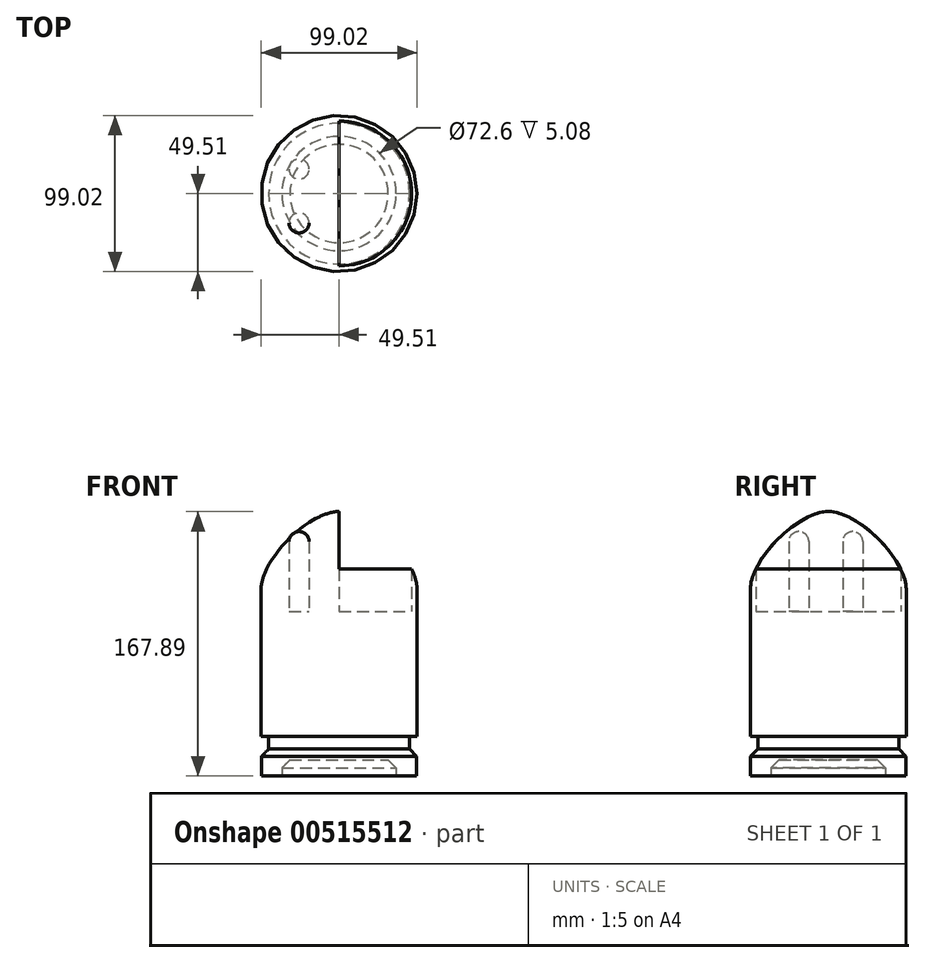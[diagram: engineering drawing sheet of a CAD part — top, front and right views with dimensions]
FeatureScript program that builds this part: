
annotation { "Feature Type Name" : "Feature", "Feature Type Description" : "" }
export const myFeature = defineFeature(function(context is Context, id is Id, definition is map)
    precondition{}
    {
        {
            var Q0;
            Q0=qCreatedBy(makeId("Top.planeOp"),FACE);
            var sketch = newSketch(context, id + "F0", { "sketchPlane" : qUnion([Q0])});
            skCircle(sketch, "E0", {"center": v(0, 0) * mm, "radius": 49.51 * mm});
            skSolve(sketch);
        }
        {
            var Q0;
            Q0=makeQuery(id+"F0.imprint","IMPRINT",FACE,{"disambiguationData":[TD([[makeQuery(id+"F0.imprint","IMPRINT",EDGE,{"derivedFrom":sQuery(id+"F0.wireOp",EDGE,"E0")}),1.0]])]});
            extrude(context, id + "F1", {"entities" : qUnion([Q0]), "endBound" : BoundingType.SYMMETRIC, "depth" : 127 * mm, "offsetDistance" : 25.4 * mm});
        }
        {
            var Q0;
            Q0=makeQuery(id+"F1.opExtrude","CAP_EDGE",EDGE,{"disambiguationData":[OSD([sQuery(id+"F0.wireOp",EDGE,"E0")])],"isStart":false});
            fillet(context, id + "F2", {"entities" : qUnion([Q0]), "radius" : 49.28 * mm, "tangentPropagation" : true, "rho" : .29, "crossSection" : FilletCrossSection.CONIC, "allowEdgeOverflow" : false});
        }
        {
            var Q0;
            Q0=makeQuery(id+"F1.opExtrude","CAP_FACE",FACE,{"disambiguationData":[OSD([sQuery(id+"F0.wireOp",EDGE,"E0")])],"isStart":true});
            extrude(context, id + "F3", {"entities" : qUnion([Q0]), "operationType" : NewBodyOperationType.ADD, "depth" : 15.75 * mm, "offsetDistance" : 25.4 * mm});
        }
        {
            var Q0;
            Q0=makeQuery(id+"F3.opExtrude","CAP_FACE",FACE,{"disambiguationData":[OSD([sQuery(id+"F0.wireOp",EDGE,"E0")])],"isStart":false});
            var sketch = newSketch(context, id + "F4", { "sketchPlane" : qUnion([Q0])});
            skCircle(sketch, "E1", {"center": v(0, 0) * mm, "radius": 44.75 * mm});
            skSolve(sketch);
        }
        {
            var Q0;
            Q0=makeQuery(id+"F4.imprint","IMPRINT",FACE,{"disambiguationData":[TD([[makeQuery(id+"F4.imprint","IMPRINT",EDGE,{"derivedFrom":sQuery(id+"F4.wireOp",EDGE,"E1")}),1.0]])]});
            extrude(context, id + "F5", {"entities" : qUnion([Q0]), "operationType" : NewBodyOperationType.ADD, "depth" : 7.62 * mm, "offsetDistance" : 25.4 * mm});
        }
        {
            var Q0;
            Q0=makeQuery(id+"F5.opExtrude","CAP_FACE",FACE,{"disambiguationData":[OSD([sQuery(id+"F4.wireOp",EDGE,"E1")])],"isStart":false});
            var sketch = newSketch(context, id + "F6", { "sketchPlane" : qUnion([Q0])});
            skCircle(sketch, "E2", {"center": v(0, 0) * mm, "radius": 49.32 * mm});
            skSolve(sketch);
        }
        {
            var Q0;
            Q0=makeQuery(id+"F6.imprint","IMPRINT",FACE,{"disambiguationData":[TD([[makeQuery(id+"F6.imprint","IMPRINT",EDGE,{"derivedFrom":makeQuery(id+"F5.opExtrude","CAP_EDGE",EDGE,{"disambiguationData":[OSD([sQuery(id+"F4.wireOp",EDGE,"E1")])],"isStart":false})}),1.0]])]});
            var Q1;
            Q1=makeQuery(id+"F6.imprint","IMPRINT",FACE,{"disambiguationData":[TD([[makeQuery(id+"F6.imprint","IMPRINT",EDGE,{"derivedFrom":sQuery(id+"F6.wireOp",EDGE,"E2")}),1.0]])]});
            extrude(context, id + "F7", {"entities" : qUnion([Q0, Q1]), "operationType" : NewBodyOperationType.ADD, "depth" : 17.53 * mm, "offsetDistance" : 25.4 * mm});
        }
        {
            var Q0;
            Q0=makeQuery(id+"F7.opExtrude","CAP_EDGE",EDGE,{"disambiguationData":[OSD([sQuery(id+"F6.wireOp",EDGE,"E2")])],"isStart":true});
            chamfer(context, id + "F8", {"entities" : qUnion([Q0]), "width" : 5.08 * mm, "tangentPropagation" : true});
        }
        {
            var Q0;
            Q0=makeQuery(id+"F7.opExtrude","CAP_FACE",FACE,{"disambiguationData":[OSD([sQuery(id+"F6.wireOp",EDGE,"E2")])],"isStart":false});
            var sketch = newSketch(context, id + "F9", { "sketchPlane" : qUnion([Q0])});
            skCircle(sketch, "E3", {"center": v(0, 0) * mm, "radius": 36.3 * mm});
            skSolve(sketch);
        }
        {
            var Q0;
            Q0=makeQuery(id+"F9.imprint","IMPRINT",FACE,{"disambiguationData":[TD([[makeQuery(id+"F9.imprint","IMPRINT",EDGE,{"derivedFrom":sQuery(id+"F9.wireOp",EDGE,"E3")}),1.0]])]});
            extrude(context, id + "F10", {"entities" : qUnion([Q0]), "operationType" : NewBodyOperationType.REMOVE, "oppositeDirection" : true, "depth" : 10.16 * mm, "offsetDistance" : 25.4 * mm});
        }
        {
            var Q0;
            Q0=makeQuery(id+"F10.boolean.opBoolean","COPY",EDGE,{"derivedFrom":makeQuery(id+"F10.opExtrude","CAP_EDGE",EDGE,{"disambiguationData":[OSD([sQuery(id+"F9.wireOp",EDGE,"E3")])],"isStart":false})});
            var Q1;
            Q1=makeQuery(id+"F10.boolean.opBoolean","COPY",EDGE,{"derivedFrom":makeQuery(id+"F10.opExtrude","CAP_EDGE",EDGE,{"disambiguationData":[OSD([sQuery(id+"F9.wireOp",EDGE,"E3")])],"isStart":true})});
            chamfer(context, id + "F11", {"entities" : qUnion([Q0, Q1]), "width" : 5.08 * mm, "tangentPropagation" : true});
        }
        {
            var Q0;
            Q0=qCreatedBy(makeId("Top.planeOp"),FACE);
            var sketch = newSketch(context, id + "F12", { "sketchPlane" : qUnion([Q0])});
            skLineSegment(sketch, "E4", {"start": v(0, -45.98) * mm, "end": v(0, 45.98) * mm});
            skArc(sketch, "E5", {"start": v(0, -45.98) * mm, "mid": v(45.98, 0) * mm, "end": v(0, 45.98) * mm});
            skSolve(sketch);
        }
        {
            var Q0;
            Q0 = qSketchRegion(id + "F12", true);
            extrude(context, id + "F13", {"entities" : qUnion([Q0]), "operationType" : NewBodyOperationType.REMOVE, "endBound" : BoundingType.THROUGH_ALL, "depth" : 25.4 * mm, "offsetDistance" : 25.4 * mm});
        }
        {
            var Q0;
            Q0=makeQuery(id+"F13.boolean.opBoolean","COPY",FACE,{"derivedFrom":makeQuery(id+"F13.opExtrude","CAP_FACE",FACE,{"disambiguationData":[OSD([sQuery(id+"F12.wireOp",EDGE,"E4"),sQuery(id+"F12.wireOp",EDGE,"E5")])],"isStart":true})});
            var sketch = newSketch(context, id + "F14", { "sketchPlane" : qUnion([Q0])});
            skCircle(sketch, "E6", {"center": v(-25.4, -18.7) * mm, "radius": 6.35 * mm});
            skCircle(sketch, "E7", {"center": v(-25.4, 15.53) * mm, "radius": 6.35 * mm});
            skLineSegment(sketch, "E8", {"start": v(-25.4, -18.7) * mm, "end": v(-25.4, 15.53) * mm, "construction": true});
            skSolve(sketch);
        }
        {
            var Q0;
            Q0=makeQuery(id+"F14.imprint","IMPRINT",FACE,{"disambiguationData":[TD([[makeQuery(id+"F14.imprint","IMPRINT",EDGE,{"derivedFrom":sQuery(id+"F14.wireOp",EDGE,"E7")}),1.0]])]});
            var Q1;
            Q1=makeQuery(id+"F14.imprint","IMPRINT",FACE,{"disambiguationData":[TD([[makeQuery(id+"F14.imprint","IMPRINT",EDGE,{"derivedFrom":sQuery(id+"F14.wireOp",EDGE,"E6")}),1.0]])]});
            extrude(context, id + "F15", {"entities" : qUnion([Q0, Q1]), "depth" : 50.8 * mm, "offsetDistance" : 25.4 * mm});
        }
        {
            var Q0;
            Q0=makeQuery(id+"F15.opExtrude","CAP_EDGE",EDGE,{"disambiguationData":[OSD([sQuery(id+"F14.wireOp",EDGE,"E7")])],"isStart":false});
            var Q1;
            Q1=makeQuery(id+"F15.opExtrude","CAP_EDGE",EDGE,{"disambiguationData":[OSD([sQuery(id+"F14.wireOp",EDGE,"E6")])],"isStart":false});
            fillet(context, id + "F16", {"entities" : qUnion([Q0, Q1]), "radius" : 6.35 * mm, "tangentPropagation" : true, "allowEdgeOverflow" : false});
        }
    });
